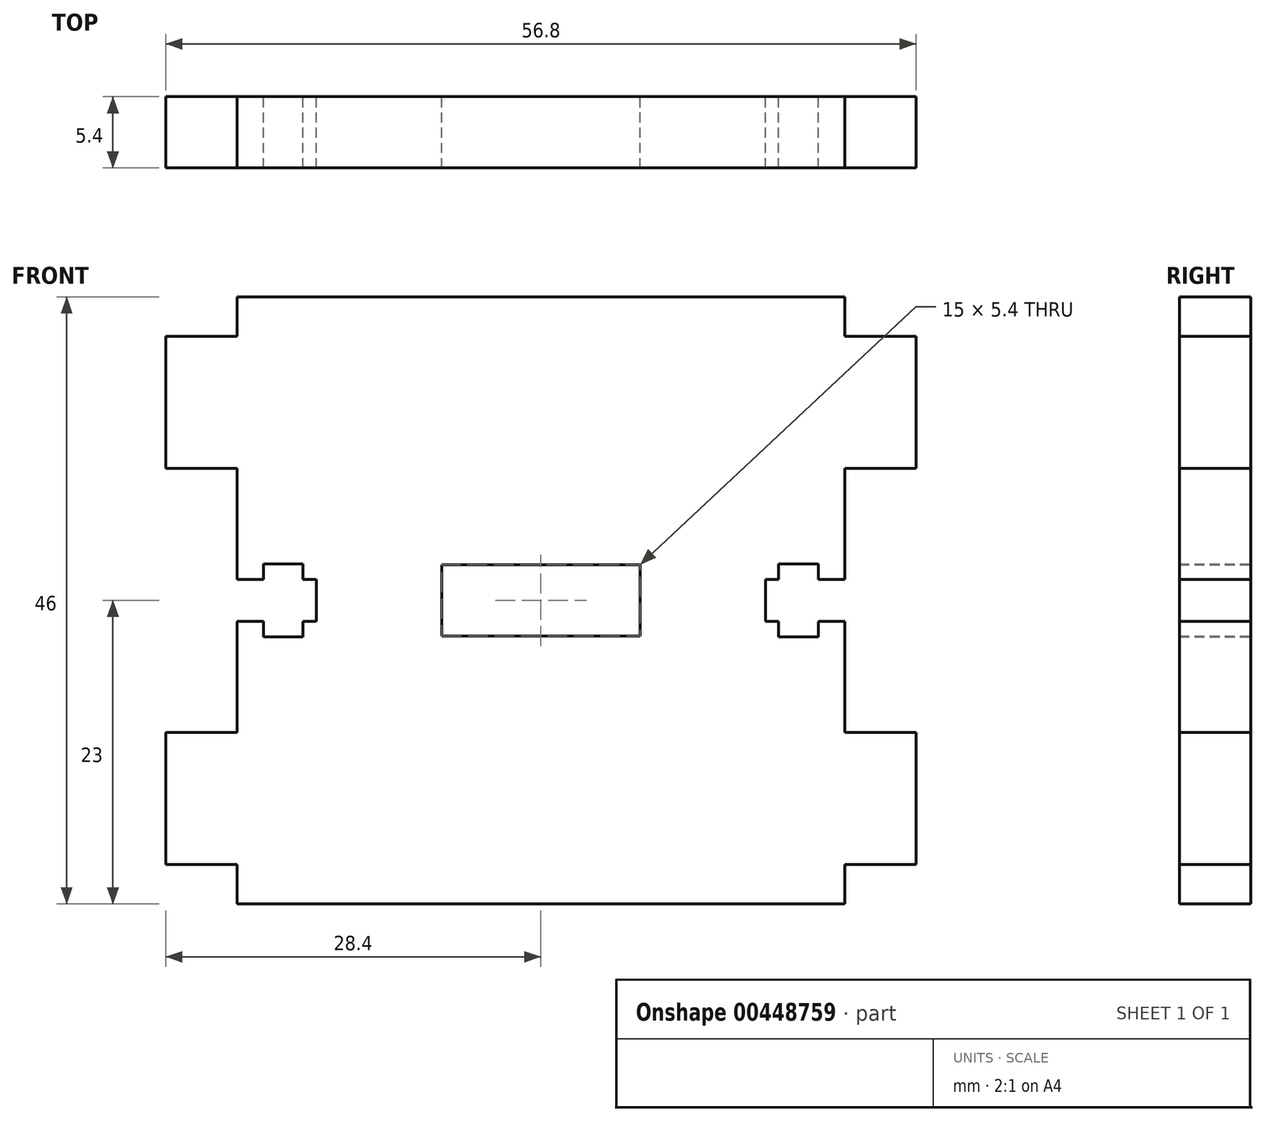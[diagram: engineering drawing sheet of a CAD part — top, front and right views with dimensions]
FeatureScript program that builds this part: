
annotation { "Feature Type Name" : "Feature", "Feature Type Description" : "" }
export const myFeature = defineFeature(function(context is Context, id is Id, definition is map)
    precondition{}
    {
        {
            assignVariable(context, id + "F0", {"name" : "thickness", "anyValue" : 5.4 * mm});
        }
        {
            var Q0;
            Q0=qCreatedBy(makeId("Front.planeOp"),FACE);
            var sketch = newSketch(context, id + "F1", { "sketchPlane" : qUnion([Q0])});
            skLineSegment(sketch, "E0.bottom", {"start": v(0, 0) * mm, "end": v(46, 0) * mm});
            skLineSegment(sketch, "E0.top", {"start": v(0, 46) * mm, "end": v(46, 46) * mm});
            skLineSegment(sketch, "E0.left", {"start": v(0, 0) * mm, "end": v(0, 3) * mm});
            skLineSegment(sketch, "E0.right", {"start": v(46, 0) * mm, "end": v(46, 3) * mm});
            skLineSegment(sketch, "E1", {"start": v(0, 43) * mm, "end": v(-5.4, 43) * mm});
            skLineSegment(sketch, "E2", {"start": v(-5.4, 43) * mm, "end": v(-5.4, 33) * mm});
            skLineSegment(sketch, "E3", {"start": v(-5.4, 33) * mm, "end": v(0, 33) * mm});
            skLineSegment(sketch, "E4", {"start": v(0, 23) * mm, "end": v(46, 23) * mm, "construction": true});
            skLineSegment(sketch, "E5", {"start": v(0, 24.6) * mm, "end": v(2, 24.6) * mm});
            skLineSegment(sketch, "E6", {"start": v(2, 24.6) * mm, "end": v(2, 25.75) * mm});
            skLineSegment(sketch, "E7", {"start": v(2, 25.75) * mm, "end": v(5, 25.75) * mm});
            skLineSegment(sketch, "E8", {"start": v(5, 25.75) * mm, "end": v(5, 24.6) * mm});
            skLineSegment(sketch, "E9", {"start": v(5, 24.6) * mm, "end": v(6, 24.6) * mm});
            skLineSegment(sketch, "E10", {"start": v(6, 24.6) * mm, "end": v(6, 23) * mm});
            skLineSegment(sketch, "E11.MirrorCS", {"start": v(-5.4, 3) * mm, "end": v(-5.4, 13) * mm});
            skLineSegment(sketch, "E12.MirrorCS", {"start": v(-5.4, 13) * mm, "end": v(0, 13) * mm});
            skLineSegment(sketch, "E13.MirrorCS", {"start": v(0, 3) * mm, "end": v(-5.4, 3) * mm});
            skLineSegment(sketch, "E14.MirrorCS", {"start": v(5, 21.4) * mm, "end": v(6, 21.4) * mm});
            skLineSegment(sketch, "E15.MirrorCS", {"start": v(5, 20.25) * mm, "end": v(5, 21.4) * mm});
            skLineSegment(sketch, "E16.MirrorCS", {"start": v(2, 20.25) * mm, "end": v(5, 20.25) * mm});
            skLineSegment(sketch, "E17.MirrorCS", {"start": v(2, 21.4) * mm, "end": v(2, 20.25) * mm});
            skLineSegment(sketch, "E18.MirrorCS", {"start": v(6, 21.4) * mm, "end": v(6, 23) * mm});
            skLineSegment(sketch, "E19.MirrorCS", {"start": v(0, 21.4) * mm, "end": v(2, 21.4) * mm});
            skLineSegment(sketch, "E20.trimOffspring", {"start": v(0, 24.6) * mm, "end": v(0, 33) * mm});
            skLineSegment(sketch, "E21.trimOffspring", {"start": v(0, 43) * mm, "end": v(0, 46) * mm});
            skLineSegment(sketch, "E22.trimOffspring", {"start": v(0, 13) * mm, "end": v(0, 21.4) * mm});
            skLineSegment(sketch, "E23", {"start": v(0, 24.6) * mm, "end": v(0, 21.4) * mm, "construction": true});
            skLineSegment(sketch, "E24", {"start": v(23, 46) * mm, "end": v(23, 0) * mm, "construction": true});
            skLineSegment(sketch, "E25.MirrorCS", {"start": v(51.4, 43) * mm, "end": v(51.4, 33) * mm});
            skLineSegment(sketch, "E26.MirrorCS", {"start": v(51.4, 33) * mm, "end": v(46, 33) * mm});
            skLineSegment(sketch, "E27.MirrorCS", {"start": v(46, 43) * mm, "end": v(51.4, 43) * mm});
            skLineSegment(sketch, "E28.MirrorCS", {"start": v(41, 20.25) * mm, "end": v(41, 21.4) * mm});
            skLineSegment(sketch, "E29.MirrorCS", {"start": v(41, 24.6) * mm, "end": v(40, 24.6) * mm});
            skLineSegment(sketch, "E30.MirrorCS", {"start": v(41, 25.75) * mm, "end": v(41, 24.6) * mm});
            skLineSegment(sketch, "E31.MirrorCS", {"start": v(44, 24.6) * mm, "end": v(44, 25.75) * mm});
            skLineSegment(sketch, "E32.MirrorCS", {"start": v(46, 24.6) * mm, "end": v(44, 24.6) * mm});
            skLineSegment(sketch, "E33.MirrorCS", {"start": v(46, 21.4) * mm, "end": v(44, 21.4) * mm});
            skLineSegment(sketch, "E34.MirrorCS", {"start": v(44, 21.4) * mm, "end": v(44, 20.25) * mm});
            skLineSegment(sketch, "E35.MirrorCS", {"start": v(40, 21.4) * mm, "end": v(40, 23) * mm});
            skLineSegment(sketch, "E36.MirrorCS", {"start": v(41, 21.4) * mm, "end": v(40, 21.4) * mm});
            skLineSegment(sketch, "E37.MirrorCS", {"start": v(40, 24.6) * mm, "end": v(40, 23) * mm});
            skLineSegment(sketch, "E38.MirrorCS", {"start": v(44, 25.75) * mm, "end": v(41, 25.75) * mm});
            skLineSegment(sketch, "E39.MirrorCS", {"start": v(44, 20.25) * mm, "end": v(41, 20.25) * mm});
            skLineSegment(sketch, "E40.MirrorCS", {"start": v(51.4, 3) * mm, "end": v(51.4, 13) * mm});
            skLineSegment(sketch, "E41.MirrorCS", {"start": v(51.4, 13) * mm, "end": v(46, 13) * mm});
            skLineSegment(sketch, "E42.MirrorCS", {"start": v(46, 3) * mm, "end": v(51.4, 3) * mm});
            skLineSegment(sketch, "E43.trimOffspring", {"start": v(46, 43) * mm, "end": v(46, 46) * mm});
            skLineSegment(sketch, "E44.trimOffspring", {"start": v(46, 13) * mm, "end": v(46, 21.4) * mm});
            skLineSegment(sketch, "E45.trimOffspring", {"start": v(46, 24.6) * mm, "end": v(46, 33) * mm});
            skLineSegment(sketch, "E46.bottom", {"start": v(15.5, 25.7) * mm, "end": v(30.5, 25.7) * mm});
            skLineSegment(sketch, "E46.top", {"start": v(15.5, 20.3) * mm, "end": v(30.5, 20.3) * mm});
            skLineSegment(sketch, "E46.left", {"start": v(15.5, 25.7) * mm, "end": v(15.5, 20.3) * mm});
            skLineSegment(sketch, "E46.right", {"start": v(30.5, 25.7) * mm, "end": v(30.5, 20.3) * mm});
            skPoint(sketch, "E47", {"position": v(30.5, 23) * mm});
            skPoint(sketch, "E48", {"position": v(23, 20.3) * mm});
            skSolve(sketch);
        }
        {
            var Q0;
            Q0=qSketchRegion(id+"F1",true);
            extrude(context, id + "F2", {"entities" : qUnion([Q0]), "depth" : getVariable(context, 'thickness')});
        }
    });
